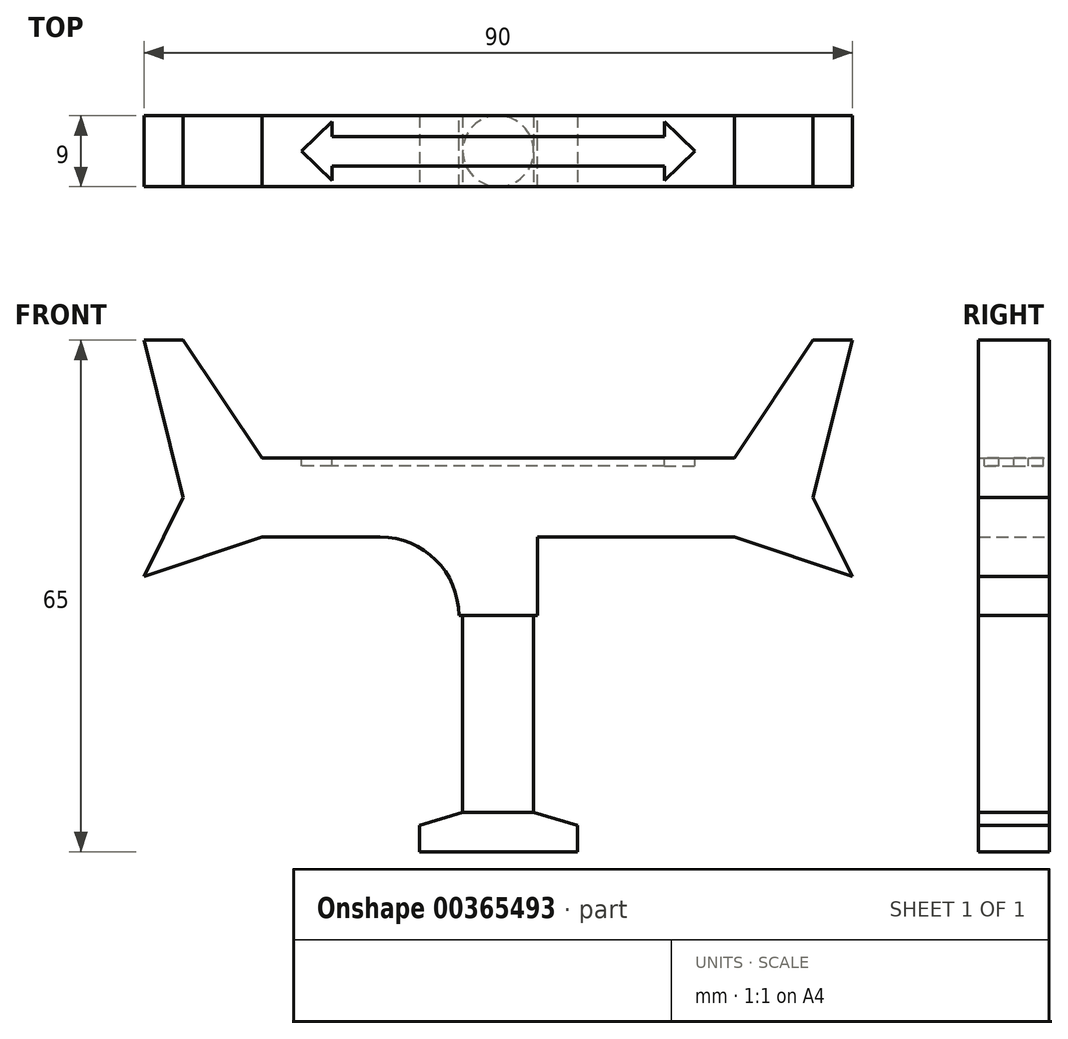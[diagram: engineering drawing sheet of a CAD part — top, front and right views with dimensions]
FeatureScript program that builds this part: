
annotation { "Feature Type Name" : "Feature", "Feature Type Description" : "" }
export const myFeature = defineFeature(function(context is Context, id is Id, definition is map)
    precondition{}
    {
        {
            var Q0;
            Q0=qCreatedBy(makeId("Front.planeOp"),FACE);
            var sketch = newSketch(context, id + "F0", { "sketchPlane" : qUnion([Q0])});
            skLineSegment(sketch, "E0", {"start": v(0, 3.73) * mm, "end": v(-30, 3.73) * mm});
            skLineSegment(sketch, "E1", {"start": v(-30, 3.73) * mm, "end": v(-40, 18.73) * mm});
            skLineSegment(sketch, "E2", {"start": v(-40, 18.73) * mm, "end": v(-45, 18.73) * mm});
            skLineSegment(sketch, "E3", {"start": v(-45, 18.73) * mm, "end": v(-40, -1.27) * mm});
            skLineSegment(sketch, "E4", {"start": v(-40, -1.27) * mm, "end": v(-45, -11.27) * mm});
            skLineSegment(sketch, "E5", {"start": v(-45, -11.27) * mm, "end": v(-30, -6.27) * mm});
            skLineSegment(sketch, "E6", {"start": v(-30, -6.27) * mm, "end": v(0, -6.27) * mm});
            skLineSegment(sketch, "E7", {"start": v(0, 3.73) * mm, "end": v(30, 3.73) * mm});
            skLineSegment(sketch, "E8", {"start": v(30, 3.73) * mm, "end": v(40, 18.73) * mm});
            skLineSegment(sketch, "E9", {"start": v(40, 18.73) * mm, "end": v(45, 18.73) * mm});
            skLineSegment(sketch, "E10", {"start": v(45, 18.73) * mm, "end": v(40, -1.27) * mm});
            skLineSegment(sketch, "E11", {"start": v(40, -1.27) * mm, "end": v(45, -11.27) * mm});
            skLineSegment(sketch, "E12", {"start": v(45, -11.27) * mm, "end": v(30, -6.27) * mm});
            skLineSegment(sketch, "E13", {"start": v(30, -6.27) * mm, "end": v(0, -6.27) * mm});
            skSolve(sketch);
        }
        {
            var Q0;
            Q0 = qSketchRegion(id + "F0", true);
            extrude(context, id + "F1", {"entities" : qUnion([Q0]), "depth" : 9 * mm});
        }
        {
            var Q0;
            Q0=makeQuery(id+"F1.opExtrude","SWEPT_FACE",FACE,{"disambiguationData":[OSD([sQuery(id+"F0.wireOp",EDGE,"E0"),sQuery(id+"F0.wireOp",EDGE,"E7")])]});
            var sketch = newSketch(context, id + "F2", { "sketchPlane" : qUnion([Q0])});
            skPoint(sketch, "E14.startSnap0", {"position": v(-30, -4.5) * mm});
            skPoint(sketch, "E14.startSnap1", {"position": v(0, 0) * mm});
            skLineSegment(sketch, "E15", {"start": v(25, -4.5) * mm, "end": v(-25, -4.5) * mm});
            skLineSegment(sketch, "E16", {"start": v(25, -4.5) * mm, "end": v(21.11, -4.5) * mm});
            skLineSegment(sketch, "E17", {"start": v(-25, -4.5) * mm, "end": v(-21.1, -4.5) * mm});
            skLineSegment(sketch, "E18", {"start": v(21.11, -4.5) * mm, "end": v(21.11, -8.25) * mm});
            skLineSegment(sketch, "E19", {"start": v(21.11, -8.25) * mm, "end": v(25, -4.5) * mm});
            skLineSegment(sketch, "E20", {"start": v(25, -4.5) * mm, "end": v(21.11, -0.75) * mm});
            skLineSegment(sketch, "E21", {"start": v(21.11, -0.75) * mm, "end": v(21.11, -4.5) * mm});
            skLineSegment(sketch, "E22", {"start": v(-21.1, -4.5) * mm, "end": v(-21.1, -8.25) * mm});
            skLineSegment(sketch, "E23", {"start": v(-21.1, -8.25) * mm, "end": v(-25, -4.5) * mm});
            skLineSegment(sketch, "E24", {"start": v(-21.11, -4.5) * mm, "end": v(-21.11, -0.75) * mm});
            skLineSegment(sketch, "E25", {"start": v(-21.11, -0.75) * mm, "end": v(-25, -4.5) * mm});
            skLineSegment(sketch, "E26", {"start": v(21.11, -6.37) * mm, "end": v(-21.11, -6.38) * mm});
            skLineSegment(sketch, "E27", {"start": v(21.11, -2.62) * mm, "end": v(-21.11, -2.63) * mm});
            skSolve(sketch);
        }
        {
            var Q0;
            Q0 = qSketchRegion(id + "F2", true);
            extrude(context, id + "F3", {"entities" : qUnion([Q0]), "operationType" : NewBodyOperationType.REMOVE, "oppositeDirection" : true, "depth" : 1 * mm});
        }
        {
            var Q0;
            Q0=makeQuery(id+"F1.opExtrude","SWEPT_FACE",FACE,{"disambiguationData":[OSD([sQuery(id+"F0.wireOp",EDGE,"E6"),sQuery(id+"F0.wireOp",EDGE,"E13")])]});
            var sketch = newSketch(context, id + "F4", { "sketchPlane" : qUnion([Q0])});
            skLineSegment(sketch, "E28", {"start": v(-5, 9) * mm, "end": v(-5, 0) * mm});
            skLineSegment(sketch, "E29", {"start": v(5, 9) * mm, "end": v(5, 0) * mm});
            skSolve(sketch);
        }
        {
            var Q0;
            Q0 = qSketchRegion(id + "F4", true);
            var Q1;
            {var subQ0=sQuery(id+"F4.wireOp",EDGE,"E28");Q1=makeQuery(id+"F4.imprint","IMPRINT",FACE,{"disambiguationData":[TD([[makeQuery(id+"F4.imprint","IMPRINT",EDGE,{"derivedFrom":subQ0}),1.0]])]});}
            extrude(context, id + "F5", {"entities" : qUnion([Q0, Q1]), "operationType" : NewBodyOperationType.ADD, "depth" : 10 * mm});
        }
        {
            var Q0;
            Q0=makeQuery(id+"F5.opExtrude","CAP_EDGE",EDGE,{"disambiguationData":[OSD([sQuery(id+"F4.wireOp",EDGE,"E29")])],"isStart":true});
            var Q1;
            Q1=makeQuery(id+"F5.opExtrude","CAP_EDGE",EDGE,{"disambiguationData":[OSD([sQuery(id+"F4.wireOp",EDGE,"E28")])],"isStart":true});
            fillet(context, id + "F6", {"entities" : qUnion([Q0, Q1]), "radius" : 10 * mm, "tangentPropagation" : true, "allowEdgeOverflow" : false});
        }
        {
            var Q0;
            Q0=makeQuery(id+"F5.opExtrude","CAP_FACE",FACE,{"disambiguationData":[OSD([sQuery(id+"F0.wireOp",EDGE,"E6"),sQuery(id+"F0.wireOp",EDGE,"E13"),sQuery(id+"F4.wireOp",EDGE,"E28"),sQuery(id+"F4.wireOp",EDGE,"E29")])],"isStart":false});
            var sketch = newSketch(context, id + "F7", { "sketchPlane" : qUnion([Q0])});
            skCircle(sketch, "E30", {"center": v(0, 4.5) * mm, "radius": 4.5 * mm});
            skPoint(sketch, "E30.centerSnap0", {"position": v(-5, 4.5) * mm});
            skPoint(sketch, "E30.centerSnap1", {"position": v(0, 9) * mm});
            skSolve(sketch);
        }
        {
            var Q0;
            Q0 = qSketchRegion(id + "F7", true);
            extrude(context, id + "F8", {"entities" : qUnion([Q0]), "operationType" : NewBodyOperationType.ADD, "depth" : 25 * mm});
        }
        {
            var Q0;
            Q0=makeQuery(id+"F8.opExtrude","CAP_FACE",FACE,{"disambiguationData":[OSD([sQuery(id+"F7.wireOp",EDGE,"E30")])],"isStart":false});
            var sketch = newSketch(context, id + "F9", { "sketchPlane" : qUnion([Q0])});
            skLineSegment(sketch, "E31", {"start": v(0, 0) * mm, "end": v(-10, 0) * mm});
            skLineSegment(sketch, "E32", {"start": v(-10, 0) * mm, "end": v(-10, 9) * mm});
            skLineSegment(sketch, "E33", {"start": v(-10, 9) * mm, "end": v(0, 9) * mm});
            skLineSegment(sketch, "E34", {"start": v(0, 9) * mm, "end": v(10.08, 9) * mm});
            skLineSegment(sketch, "E35", {"start": v(10.08, 9) * mm, "end": v(10.08, 0) * mm});
            skLineSegment(sketch, "E36", {"start": v(10.08, 0) * mm, "end": v(0, 0) * mm});
            skSolve(sketch);
        }
        {
            var Q0;
            Q0 = qSketchRegion(id + "F9", true);
            extrude(context, id + "F10", {"entities" : qUnion([Q0]), "operationType" : NewBodyOperationType.ADD, "depth" : 5 * mm});
        }
        {
            var Q0;
            Q0=makeQuery(id+"F10.opExtrude","SWEPT_FACE",FACE,{"disambiguationData":[OSD([sQuery(id+"F9.wireOp",EDGE,"E33"),sQuery(id+"F9.wireOp",EDGE,"E34")])]});
            var sketch = newSketch(context, id + "F11", { "sketchPlane" : qUnion([Q0])});
            skLineSegment(sketch, "E37", {"start": v(-10, -42.94) * mm, "end": v(-4.54, -41.27) * mm});
            skLineSegment(sketch, "E38", {"start": v(-4.54, -41.27) * mm, "end": v(4.51, -41.27) * mm});
            skLineSegment(sketch, "E39", {"start": v(4.51, -41.27) * mm, "end": v(10.08, -42.94) * mm});
            skSolve(sketch);
        }
        {
            var Q0;
            Q0 = qSketchRegion(id + "F11", true);
            var Q1;
            {var subQ0=sQuery(id+"F11.wireOp",EDGE,"E37");Q1=makeQuery(id+"F11.imprint","IMPRINT",FACE,{"disambiguationData":[TD([[makeQuery(id+"F11.imprint","IMPRINT",EDGE,{"derivedFrom":subQ0}),1.0]])]});}
            var Q2;
            {var subQ0=sQuery(id+"F11.wireOp",EDGE,"E39");Q2=makeQuery(id+"F11.imprint","IMPRINT",FACE,{"disambiguationData":[TD([[makeQuery(id+"F11.imprint","IMPRINT",EDGE,{"derivedFrom":subQ0}),1.0]])]});}
            extrude(context, id + "F12", {"entities" : qUnion([Q0, Q1, Q2]), "operationType" : NewBodyOperationType.REMOVE, "oppositeDirection" : true, "depth" : 25 * mm});
        }
    });
